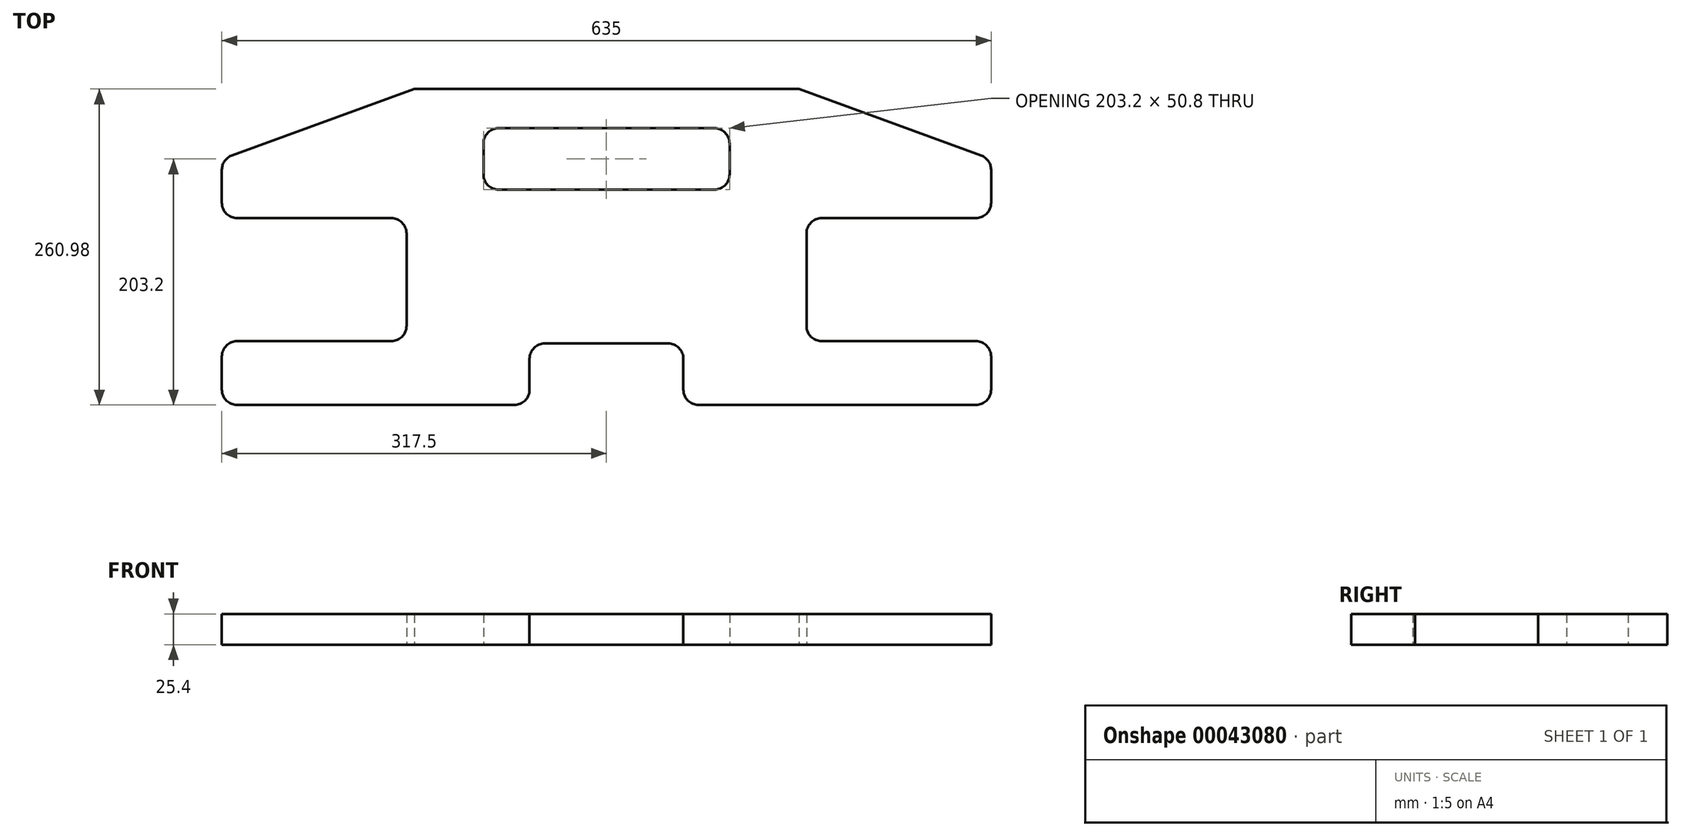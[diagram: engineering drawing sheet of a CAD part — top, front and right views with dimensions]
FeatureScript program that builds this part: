
annotation { "Feature Type Name" : "Feature", "Feature Type Description" : "" }
export const myFeature = defineFeature(function(context is Context, id is Id, definition is map)
    precondition{}
    {
        {
            var Q0;
            Q0=qCreatedBy(makeId("Top.planeOp"),FACE);
            var sketch = newSketch(context, id + "F0", { "sketchPlane" : qUnion([Q0])});
            skLineSegment(sketch, "E0.rect.bottom", {"start": v(317.5, 101.6) * mm, "end": v(-317.5, 101.6) * mm, "construction": true});
            skLineSegment(sketch, "E0.rect.top", {"start": v(304.8, -101.6) * mm, "end": v(76.2, -101.6) * mm});
            skLineSegment(sketch, "E0.rect.left", {"start": v(317.5, 92.7) * mm, "end": v(317.5, 65.4) * mm});
            skLineSegment(sketch, "E0.rect.right", {"start": v(-317.5, 92.7) * mm, "end": v(-317.5, 65.4) * mm});
            skPoint(sketch, "E0.rect.middle", {"position": v(0, 0) * mm});
            skLineSegment(sketch, "E1.rect.bottom", {"start": v(-177.8, 52.7) * mm, "end": v(-304.8, 52.7) * mm});
            skLineSegment(sketch, "E1.rect.top", {"start": v(-177.8, -48.9) * mm, "end": v(-304.8, -48.9) * mm});
            skLineSegment(sketch, "E1.rect.left", {"start": v(-165.1, 40) * mm, "end": v(-165.1, -36.2) * mm});
            skLineSegment(sketch, "E2.rect.bottom", {"start": v(177.8, 52.7) * mm, "end": v(304.8, 52.7) * mm});
            skLineSegment(sketch, "E2.rect.top", {"start": v(177.8, -48.9) * mm, "end": v(304.8, -48.9) * mm});
            skLineSegment(sketch, "E2.rect.left", {"start": v(165.1, 40) * mm, "end": v(165.1, -36.2) * mm});
            skLineSegment(sketch, "E3.trimOffspring", {"start": v(-317.5, -61.6) * mm, "end": v(-317.5, -88.9) * mm});
            skLineSegment(sketch, "E4.trimOffspring", {"start": v(317.5, -61.6) * mm, "end": v(317.5, -88.9) * mm});
            skLineSegment(sketch, "E5", {"start": v(-309.14, 104.64) * mm, "end": v(-158.75, 159.38) * mm});
            skLineSegment(sketch, "E6", {"start": v(309.14, 104.64) * mm, "end": v(158.75, 159.38) * mm});
            skLineSegment(sketch, "E7.rect.bottom", {"start": v(158.75, 159.38) * mm, "end": v(-158.75, 159.38) * mm});
            skPoint(sketch, "E7.rect.middle", {"position": v(0, 101.6) * mm});
            skLineSegment(sketch, "E8.rect.bottom", {"start": v(-88.9, 127) * mm, "end": v(88.9, 127) * mm});
            skLineSegment(sketch, "E8.rect.top", {"start": v(-88.9, 76.2) * mm, "end": v(88.9, 76.2) * mm});
            skLineSegment(sketch, "E8.rect.left", {"start": v(-101.6, 114.3) * mm, "end": v(-101.6, 88.9) * mm});
            skLineSegment(sketch, "E8.rect.right", {"start": v(101.6, 114.3) * mm, "end": v(101.6, 88.9) * mm});
            skPoint(sketch, "E9.visualSharp", {"position": v(-101.6, 127) * mm});
            skArc(sketch, "E9.filletArc", {"start": v(-88.9, 127) * mm, "mid": v(-97.88, 123.28) * mm, "end": v(-101.6, 114.3) * mm});
            skPoint(sketch, "E10.visualSharp", {"position": v(101.6, 127) * mm});
            skArc(sketch, "E10.filletArc", {"start": v(101.6, 114.3) * mm, "mid": v(97.88, 123.28) * mm, "end": v(88.9, 127) * mm});
            skPoint(sketch, "E11.visualSharp", {"position": v(101.6, 76.2) * mm});
            skArc(sketch, "E11.filletArc", {"start": v(88.9, 76.2) * mm, "mid": v(97.88, 79.92) * mm, "end": v(101.6, 88.9) * mm});
            skPoint(sketch, "E12.visualSharp", {"position": v(-101.6, 76.2) * mm});
            skArc(sketch, "E12.filletArc", {"start": v(-101.6, 88.9) * mm, "mid": v(-97.88, 79.92) * mm, "end": v(-88.9, 76.2) * mm});
            skPoint(sketch, "E13.visualSharp", {"position": v(-317.5, 101.6) * mm});
            skArc(sketch, "E13.filletArc", {"start": v(-309.14, 104.64) * mm, "mid": v(-315.2, 100) * mm, "end": v(-317.5, 92.7) * mm});
            skPoint(sketch, "E14.visualSharp", {"position": v(317.5, 101.6) * mm});
            skArc(sketch, "E14.filletArc", {"start": v(317.5, 92.7) * mm, "mid": v(315.2, 100) * mm, "end": v(309.14, 104.64) * mm});
            skPoint(sketch, "E15.visualSharp", {"position": v(317.5, 52.7) * mm});
            skArc(sketch, "E15.filletArc", {"start": v(304.8, 52.7) * mm, "mid": v(313.78, 56.42) * mm, "end": v(317.5, 65.4) * mm});
            skPoint(sketch, "E16.visualSharp", {"position": v(317.5, -48.9) * mm});
            skArc(sketch, "E16.filletArc", {"start": v(317.5, -61.6) * mm, "mid": v(313.78, -52.62) * mm, "end": v(304.8, -48.9) * mm});
            skPoint(sketch, "E17.visualSharp", {"position": v(165.1, 52.7) * mm});
            skArc(sketch, "E17.filletArc", {"start": v(177.8, 52.7) * mm, "mid": v(168.82, 48.98) * mm, "end": v(165.1, 40) * mm});
            skPoint(sketch, "E18.visualSharp", {"position": v(165.1, -48.9) * mm});
            skArc(sketch, "E18.filletArc", {"start": v(165.1, -36.2) * mm, "mid": v(168.82, -45.18) * mm, "end": v(177.8, -48.9) * mm});
            skPoint(sketch, "E19.visualSharp", {"position": v(-165.1, 52.7) * mm});
            skArc(sketch, "E19.filletArc", {"start": v(-165.1, 40) * mm, "mid": v(-168.82, 48.98) * mm, "end": v(-177.8, 52.7) * mm});
            skPoint(sketch, "E20.visualSharp", {"position": v(-165.1, -48.9) * mm});
            skArc(sketch, "E20.filletArc", {"start": v(-177.8, -48.9) * mm, "mid": v(-168.82, -45.18) * mm, "end": v(-165.1, -36.2) * mm});
            skPoint(sketch, "E21.visualSharp", {"position": v(-317.5, 52.7) * mm});
            skArc(sketch, "E21.filletArc", {"start": v(-317.5, 65.4) * mm, "mid": v(-313.78, 56.42) * mm, "end": v(-304.8, 52.7) * mm});
            skPoint(sketch, "E22.visualSharp", {"position": v(-317.5, -48.9) * mm});
            skArc(sketch, "E22.filletArc", {"start": v(-304.8, -48.9) * mm, "mid": v(-313.78, -52.62) * mm, "end": v(-317.5, -61.6) * mm});
            skPoint(sketch, "E23.visualSharp", {"position": v(-317.5, -101.6) * mm});
            skArc(sketch, "E23.filletArc", {"start": v(-317.5, -88.9) * mm, "mid": v(-313.78, -97.88) * mm, "end": v(-304.8, -101.6) * mm});
            skPoint(sketch, "E24.visualSharp", {"position": v(317.5, -101.6) * mm});
            skArc(sketch, "E24.filletArc", {"start": v(304.8, -101.6) * mm, "mid": v(313.78, -97.88) * mm, "end": v(317.5, -88.9) * mm});
            skLineSegment(sketch, "E25.rect.top", {"start": v(50.8, -50.8) * mm, "end": v(-50.8, -50.8) * mm});
            skLineSegment(sketch, "E25.rect.left", {"start": v(63.5, -88.9) * mm, "end": v(63.5, -63.5) * mm});
            skLineSegment(sketch, "E25.rect.right", {"start": v(-63.5, -88.9) * mm, "end": v(-63.5, -63.5) * mm});
            skPoint(sketch, "E25.rect.middle", {"position": v(0, -76.2) * mm});
            skPoint(sketch, "E25.rect.centerSnap0", {"position": v(0, -101.6) * mm});
            skLineSegment(sketch, "E26.trimOffspring", {"start": v(-76.2, -101.6) * mm, "end": v(-304.8, -101.6) * mm});
            skPoint(sketch, "E27.visualSharp", {"position": v(63.5, -101.6) * mm});
            skArc(sketch, "E27.filletArc", {"start": v(63.5, -88.9) * mm, "mid": v(67.22, -97.88) * mm, "end": v(76.2, -101.6) * mm});
            skPoint(sketch, "E28.visualSharp", {"position": v(-63.5, -101.6) * mm});
            skArc(sketch, "E28.filletArc", {"start": v(-76.2, -101.6) * mm, "mid": v(-67.22, -97.88) * mm, "end": v(-63.5, -88.9) * mm});
            skPoint(sketch, "E29.visualSharp", {"position": v(-63.5, -50.8) * mm});
            skArc(sketch, "E29.filletArc", {"start": v(-50.8, -50.8) * mm, "mid": v(-59.78, -54.52) * mm, "end": v(-63.5, -63.5) * mm});
            skPoint(sketch, "E30.visualSharp", {"position": v(63.5, -50.8) * mm});
            skArc(sketch, "E30.filletArc", {"start": v(63.5, -63.5) * mm, "mid": v(59.78, -54.52) * mm, "end": v(50.8, -50.8) * mm});
            skSolve(sketch);
        }
        {
            var Q0;
            Q0=makeQuery(id+"F0.imprint","IMPRINT",FACE,{"disambiguationData":[TD([[makeQuery(id+"F0.imprint","IMPRINT",EDGE,{"derivedFrom":sQuery(id+"F0.wireOp",EDGE,"E0.rect.top")}),-1.0]])]});
            extrude(context, id + "F1", {"entities" : qUnion([Q0]), "depth" : 25.4 * mm});
        }
    });
